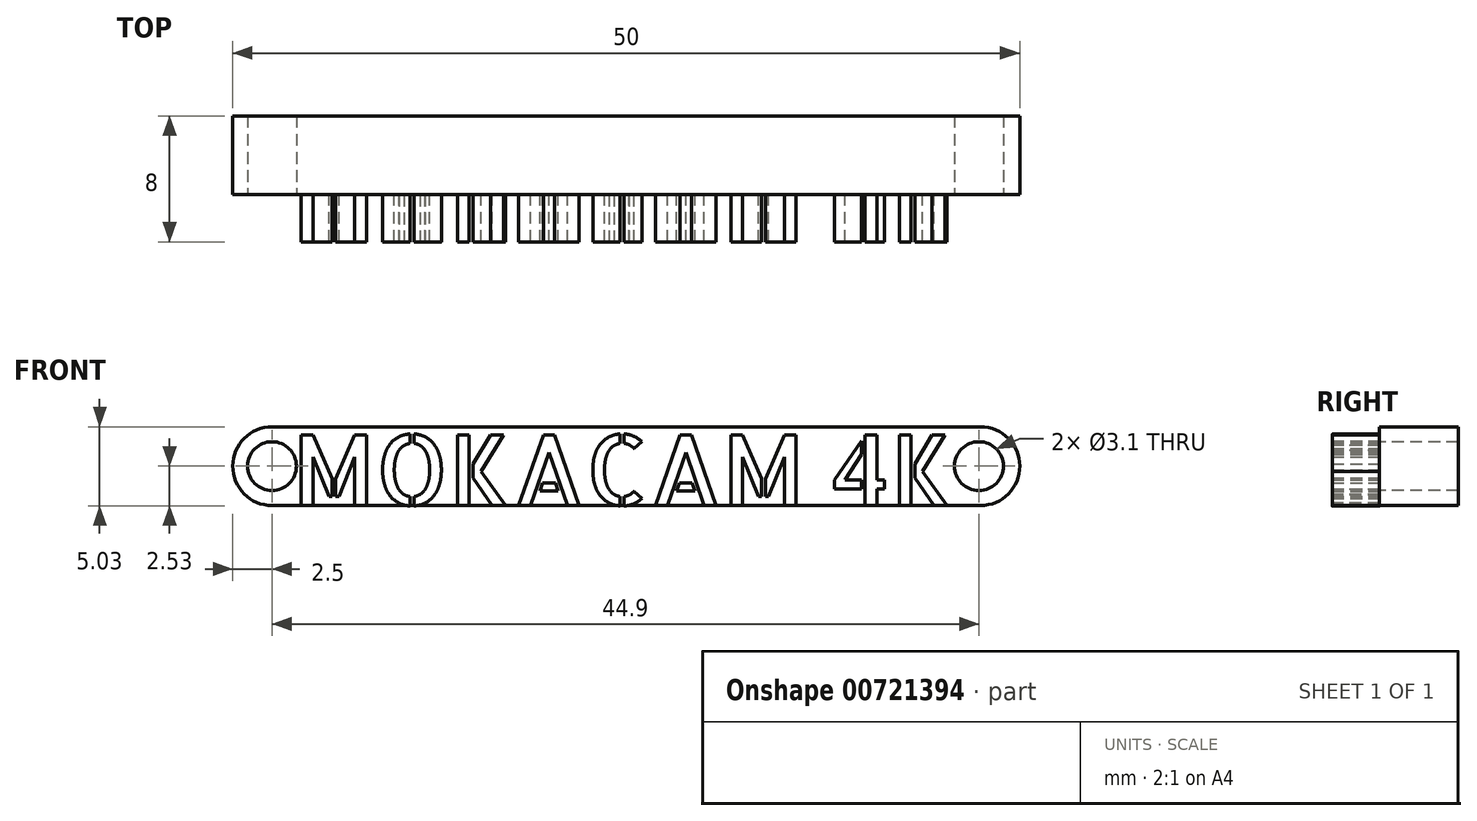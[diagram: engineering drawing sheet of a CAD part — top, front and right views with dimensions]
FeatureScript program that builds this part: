
annotation { "Feature Type Name" : "Feature", "Feature Type Description" : "" }
export const myFeature = defineFeature(function(context is Context, id is Id, definition is map)
    precondition{}
    {
        {
            var Q0;
            Q0=qCreatedBy(makeId("Front.planeOp"),FACE);
            var sketch = newSketch(context, id + "F0", { "sketchPlane" : qUnion([Q0])});
            skLineSegment(sketch, "E0.bottom", {"start": v(25, 2.5) * mm, "end": v(-25, 2.5) * mm});
            skLineSegment(sketch, "E0.top", {"start": v(25, -2.5) * mm, "end": v(-25, -2.5) * mm});
            skLineSegment(sketch, "E0.left", {"start": v(25, 2.5) * mm, "end": v(25, -2.5) * mm});
            skLineSegment(sketch, "E0.right", {"start": v(-25, 2.5) * mm, "end": v(-25, -2.5) * mm});
            skPoint(sketch, "E0.middle", {"position": v(0, 0) * mm});
            skSolve(sketch);
        }
        {
            var Q0;
            Q0 = qSketchRegion(id + "F0", true);
            extrude(context, id + "F1", {"entities" : qUnion([Q0]), "oppositeDirection" : true, "depth" : 5 * mm, "offsetDistance" : 25 * mm});
        }
        {
            var Q0;
            Q0=makeQuery(id+"F1.opExtrude","CAP_FACE",FACE,{"disambiguationData":[OSD([sQuery(id+"F0.wireOp",EDGE,"E0.bottom"),sQuery(id+"F0.wireOp",EDGE,"E0.top"),sQuery(id+"F0.wireOp",EDGE,"E0.left"),sQuery(id+"F0.wireOp",EDGE,"E0.right")])],"isStart":true});
            var sketch = newSketch(context, id + "F2", { "sketchPlane" : qUnion([Q0])});
            skText(sketch, "E1", { "text": "MOKACAM 4K", "fontName": "AllertaStencil-Regular.ttf"});
            const initialGuessF2  = {"E1": [-0.0212, -0.0025, 1, 0, 0.00448]};
            skSetInitialGuess(sketch, initialGuessF2);
            skSolve(sketch);
        }
        {
            var Q0;
            Q0 = qSketchRegion(id + "F2", true);
            extrude(context, id + "F3", {"entities" : qUnion([Q0]), "operationType" : NewBodyOperationType.ADD, "depth" : 3 * mm, "offsetDistance" : 25 * mm});
        }
        {
            var Q0;
            Q0=makeQuery(id+"F1.opExtrude","SWEPT_EDGE",EDGE,{"disambiguationData":[OSD([sQuery(id+"F0.wireOp",EDGE,"E0.bottom"),sQuery(id+"F0.wireOp",EDGE,"E0.left")])]});
            var Q1;
            Q1=makeQuery(id+"F1.opExtrude","SWEPT_EDGE",EDGE,{"disambiguationData":[OSD([sQuery(id+"F0.wireOp",EDGE,"E0.top"),sQuery(id+"F0.wireOp",EDGE,"E0.left")])]});
            var Q2;
            Q2=makeQuery(id+"F1.opExtrude","SWEPT_EDGE",EDGE,{"disambiguationData":[OSD([sQuery(id+"F0.wireOp",EDGE,"E0.bottom"),sQuery(id+"F0.wireOp",EDGE,"E0.right")])]});
            var Q3;
            Q3=makeQuery(id+"F1.opExtrude","SWEPT_EDGE",EDGE,{"disambiguationData":[OSD([sQuery(id+"F0.wireOp",EDGE,"E0.top"),sQuery(id+"F0.wireOp",EDGE,"E0.right")])]});
            fillet(context, id + "F4", {"entities" : qUnion([Q0, Q1, Q2, Q3]), "radius" : 2.5 * mm, "tangentPropagation" : true, "allowEdgeOverflow" : false});
        }
        {
            var Q0;
            {var subQ54=sQuery(id+"F0.wireOp",EDGE,"E0.top");var subQ55=sQuery(id+"F0.wireOp",EDGE,"E0.right");var subQ56=sQuery(id+"F0.wireOp",EDGE,"E0.bottom");var subQ57=sQuery(id+"F0.wireOp",EDGE,"E0.left");Q0=makeQuery(id+"F3.boolean.opBoolean","SPLIT",FACE,{"disambiguationData":[TD([makeQuery(id+"F1.opExtrude","SWEPT_FACE",FACE,{"disambiguationData":[OSD([subQ56])]})])],"derivedFrom":makeQuery(id+"F1.opExtrude","CAP_FACE",FACE,{"disambiguationData":[OSD([subQ56,subQ54,subQ57,subQ55])],"isStart":true})});}
            var sketch = newSketch(context, id + "F5", { "sketchPlane" : qUnion([Q0])});
            skCircle(sketch, "E2", {"center": v(-22.5, 0) * mm, "radius": 1.55 * mm});
            skCircle(sketch, "E3", {"center": v(22.4, 0) * mm, "radius": 1.55 * mm});
            skSolve(sketch);
        }
        {
            var Q0;
            Q0=makeQuery(id+"F5.imprint","IMPRINT",FACE,{"disambiguationData":[TD([[makeQuery(id+"F5.imprint","IMPRINT",EDGE,{"derivedFrom":sQuery(id+"F5.wireOp",EDGE,"E2")}),1.0]])]});
            var Q1;
            Q1=makeQuery(id+"F5.imprint","IMPRINT",FACE,{"disambiguationData":[TD([[makeQuery(id+"F5.imprint","IMPRINT",EDGE,{"derivedFrom":sQuery(id+"F5.wireOp",EDGE,"E3")}),1.0]])]});
            var Q2;
            Q2=sQuery(id+"F5.wireOp",EDGE,"E3");
            var Q3;
            Q3=sQuery(id+"F5.wireOp",EDGE,"E2");
            extrude(context, id + "F6", {"entities" : qUnion([Q0, Q1]), "operationType" : NewBodyOperationType.REMOVE, "surfaceEntities" : qUnion([Q2, Q3]), "oppositeDirection" : true, "depth" : 25 * mm, "offsetDistance" : 25 * mm});
        }
    });
